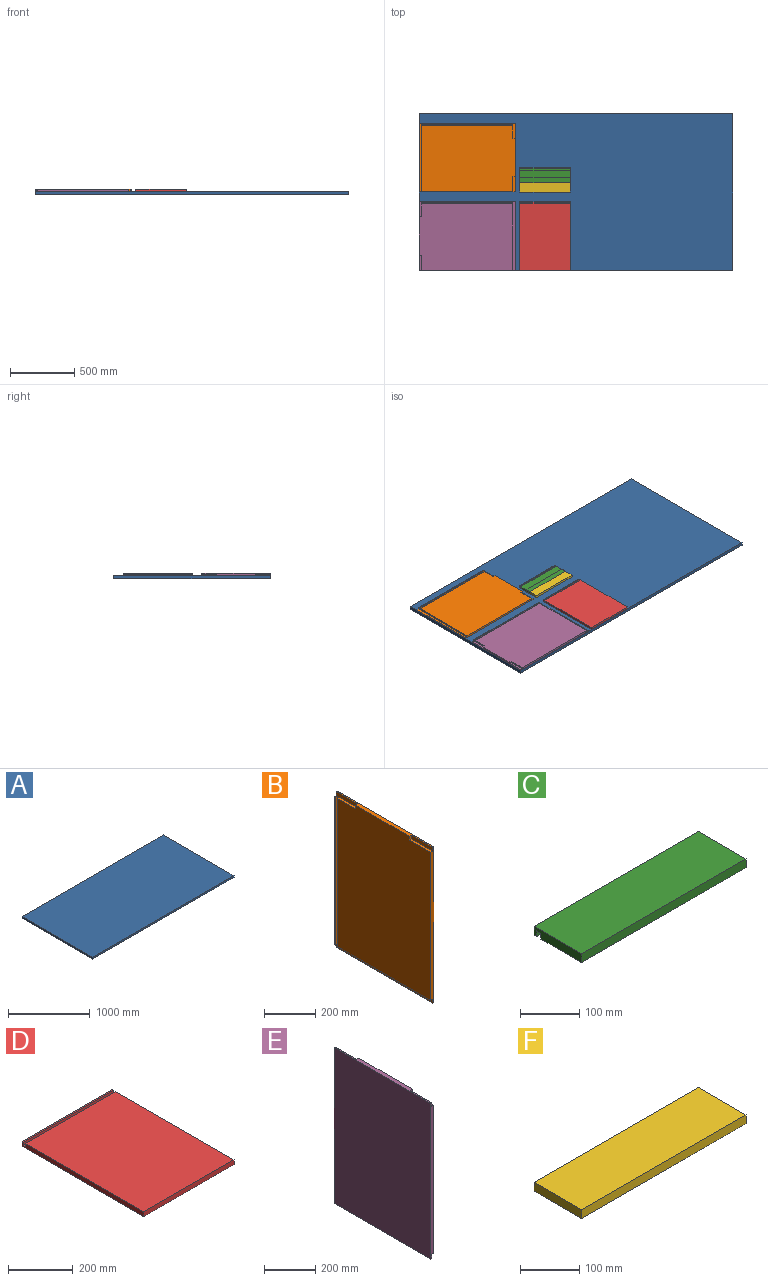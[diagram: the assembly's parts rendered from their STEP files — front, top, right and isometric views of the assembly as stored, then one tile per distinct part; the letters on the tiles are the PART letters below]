
ASSEMBLY  parts=6 mates=9
PART A: 6 faces, bbox 2438.4x1219.2x25.4 mm
  f0: plane 1219.2x25.4mm, normal (-1,0,0), area 30967.7mm2, adj f1,f3,f4,f5
  f1: plane 2438.4x25.4mm, normal (0,-1,0), area 61935.4mm2, adj f0,f2,f4,f5
  f2: plane 1219.2x25.4mm, normal (1,0,0), area 30967.7mm2, adj f1,f3,f4,f5
  f3: plane 2438.4x25.4mm, normal (0,1,0), area 61935.4mm2, adj f0,f2,f4,f5
  f4: plane 2438.4x1219.2mm, normal (0,0,-1), area 2972897.3mm2, adj f0,f1,f2,f3
  f5: plane 2438.4x1219.2mm, normal (0,0,1), area 2972897.3mm2, adj f0,f1,f2,f3
PART B: 18 faces, bbox 18.3x533.4x745.5 mm
  f0: plane 727.2x517.02mm, normal (-1,0,0), area 371978.6mm2, adj f1,f2,f4,f5,f11,f13,f14,f16
  f1: plane 517.02x11.94mm, normal (0,0,-1), area 6172.1mm2, adj f0,f4,f9,f16
  f2: plane 101.09x11.94mm, normal (0,0,1), area 1206.8mm2, adj f0,f9,f14,f16
  f3: plane 745.49x18.29mm, normal (0,1,0), area 13196.9mm2, adj f5,f6,f7,f8,f9,f10,f15
  f4: plane 745.49x18.29mm, normal (0,-1,0), area 13196.9mm2, adj f0,f1,f5,f7,f8,f9,f12,f13
  f5: plane 533.4x18.29mm, normal (0,0,1), area 6950mm2, adj f0,f3,f4,f7,f9,f11,f12,f14
  f6: plane 708.91x6.35mm, normal (-1,0,0), area 4501.6mm2, adj f3,f10,f15,f17
  f7: plane 745.49x533.4mm, normal (1,0,0), area 397644.4mm2, adj f3,f4,f5,f8
  f8: plane 533.4x6.35mm, normal (0,0,-1), area 3387.1mm2, adj f3,f4,f7,f9
  f9: plane 745.49x533.4mm, normal (-1,0,0), area 19015.7mm2, adj f1,f2,f3,f4,f5,f8,f10,f14
  f10: plane 11.94x6.35mm, normal (0,0,-1), area 75.8mm2, adj f3,f6,f9,f17
  f11: plane 18.29x11.94mm, normal (0,-1,0), area 218.3mm2, adj f0,f5,f12,f13
  f12: plane 117.48x18.29mm, normal (-1,0,0), area 2148.4mm2, adj f4,f5,f11,f13
  f13: plane 117.48x11.94mm, normal (0,0,1), area 1402.4mm2, adj f0,f4,f11,f12
  f14: plane 18.29x11.94mm, normal (0,1,0), area 218.3mm2, adj f0,f2,f5,f9
  f15: plane 11.94x6.35mm, normal (0,0,1), area 75.8mm2, adj f3,f6,f9,f17
  f16: plane 708.91x11.94mm, normal (0,1,0), area 8463mm2, adj f0,f1,f2,f9
  f17: plane 708.91x11.94mm, normal (0,-1,0), area 8463mm2, adj f6,f9,f10,f15
PART C: 10 faces, bbox 393.7x114.3x18.3 mm
  f0: plane 393.7x97.92mm, normal (0,0,-1), area 38549.9mm2, adj f2,f3,f4,f7
  f1: plane 393.7x18.29mm, normal (0,1,0), area 7200mm2, adj f2,f4,f5,f6
  f2: plane 114.3x18.29mm, normal (-1,0,0), area 1970.5mm2, adj f0,f1,f3,f5,f6,f7,f8,f9
  f3: plane 393.7x18.29mm, normal (0,-1,0), area 7200mm2, adj f0,f2,f4,f6
  f4: plane 114.3x18.29mm, normal (1,0,0), area 1970.5mm2, adj f0,f1,f3,f5,f6,f7,f8,f9
  f5: plane 393.7x6.35mm, normal (0,0,-1), area 2500mm2, adj f1,f2,f4,f8
  f6: plane 393.7x114.3mm, normal (0,0,1), area 44999.9mm2, adj f1,f2,f3,f4
  f7: plane 393.7x11.94mm, normal (0,1,0), area 4700mm2, adj f0,f2,f4,f9
  f8: plane 393.7x11.94mm, normal (0,-1,0), area 4700mm2, adj f2,f4,f5,f9
  f9: plane 393.7x10.03mm, normal (0,0,-1), area 3950mm2, adj f2,f4,f7,f8
PART D: 10 faces, bbox 393.7x533.4x18.3 mm
  f0: plane 517.02x393.7mm, normal (0,0,1), area 203549.6mm2, adj f1,f2,f3,f8
  f1: plane 533.4x18.29mm, normal (-1,0,0), area 9635mm2, adj f0,f2,f4,f5,f6,f7,f8,f9
  f2: plane 393.7x18.29mm, normal (0,-1,0), area 7200mm2, adj f0,f1,f3,f6
  f3: plane 533.4x18.29mm, normal (1,0,0), area 9635mm2, adj f0,f2,f4,f5,f6,f7,f8,f9
  f4: plane 393.7x18.29mm, normal (0,1,0), area 7200mm2, adj f1,f3,f5,f6
  f5: plane 393.7x6.35mm, normal (0,0,1), area 2500mm2, adj f1,f3,f4,f9
  f6: plane 533.4x393.7mm, normal (0,0,-1), area 209999.6mm2, adj f1,f2,f3,f4
  f7: plane 393.7x10.03mm, normal (0,0,1), area 3950mm2, adj f1,f3,f8,f9
  f8: plane 393.7x11.94mm, normal (0,1,0), area 4700mm2, adj f0,f1,f3,f7
  f9: plane 393.7x11.94mm, normal (0,-1,0), area 4700mm2, adj f1,f3,f5,f7
PART E: 18 faces, bbox 18.3x533.4x745.5 mm
  f0: plane 727.2x517.02mm, normal (1,0,0), area 371978.6mm2, adj f1,f2,f4,f7,f11,f12,f14,f16
  f1: plane 517.02x11.94mm, normal (0,0,-1), area 6172.1mm2, adj f0,f7,f10,f16
  f2: plane 101.09x11.94mm, normal (0,0,1), area 1206.8mm2, adj f0,f10,f14,f16
  f3: plane 745.49x18.29mm, normal (0,1,0), area 13196.9mm2, adj f4,f5,f6,f8,f9,f10,f15
  f4: plane 533.4x18.29mm, normal (0,0,1), area 6950mm2, adj f0,f3,f7,f8,f10,f11,f13,f14
  f5: plane 708.91x6.35mm, normal (1,0,0), area 4501.6mm2, adj f3,f9,f15,f17
  f6: plane 533.4x6.35mm, normal (0,0,-1), area 3387.1mm2, adj f3,f7,f8,f10
  f7: plane 745.49x18.29mm, normal (0,-1,0), area 13196.9mm2, adj f0,f1,f4,f6,f8,f10,f12,f13
  f8: plane 745.49x533.4mm, normal (-1,0,0), area 397644.4mm2, adj f3,f4,f6,f7
  f9: plane 11.94x6.35mm, normal (0,0,-1), area 75.8mm2, adj f3,f5,f10,f17
  f10: plane 745.49x533.4mm, normal (1,0,0), area 19015.7mm2, adj f1,f2,f3,f4,f6,f7,f9,f14
  f11: plane 18.29x11.94mm, normal (0,-1,0), area 218.3mm2, adj f0,f4,f12,f13
  f12: plane 117.48x11.94mm, normal (0,0,1), area 1402.4mm2, adj f0,f7,f11,f13
  f13: plane 117.48x18.29mm, normal (1,0,0), area 2148.4mm2, adj f4,f7,f11,f12
  f14: plane 18.29x11.94mm, normal (0,1,0), area 218.3mm2, adj f0,f2,f4,f10
  f15: plane 11.94x6.35mm, normal (0,0,1), area 75.8mm2, adj f3,f5,f10,f17
  f16: plane 708.91x11.94mm, normal (0,1,0), area 8463mm2, adj f0,f1,f2,f10
  f17: plane 708.91x11.94mm, normal (0,-1,0), area 8463mm2, adj f5,f9,f10,f15
PART F: 6 faces, bbox 393.7x114.3x18.3 mm
  f0: plane 393.7x18.29mm, normal (0,1,0), area 7200mm2, adj f1,f3,f4,f5
  f1: plane 114.3x18.29mm, normal (-1,0,0), area 2090.3mm2, adj f0,f2,f4,f5
  f2: plane 393.7x18.29mm, normal (0,-1,0), area 7200mm2, adj f1,f3,f4,f5
  f3: plane 114.3x18.29mm, normal (1,0,0), area 2090.3mm2, adj f0,f2,f4,f5
  f4: plane 393.7x114.3mm, normal (0,0,-1), area 44999.9mm2, adj f0,f1,f2,f3
  f5: plane 393.7x114.3mm, normal (0,0,1), area 44999.9mm2, adj f0,f1,f2,f3
PLACE A at identity fixed
PLACE B rot(axis=(0,1,0),90deg) t=(0,609.6,406.4)mm
PLACE C rot(axis=(0,1,0),180deg) t=(1181.88,263.46,745.49)mm
PLACE D t=(775.48,0,0)mm
PLACE E rot(axis=(0,-1,0),90deg) t=(745.49,0,0)mm
PLACE F t=(775.48,609.22,-727.2)mm
MATE planar F.f4 <-> A.f5  axis (0,0,-1) through (978.68,723.52,0)mm
MATE planar A.f1 <-> D.f2  axis (0,-1,0) through (1219.2,0,-12.7)mm
MATE slider E.f6 <-> D.f1  axis (1,0,0) through (745.49,0,0)mm
MATE fastened B.f7 <-> A.f5  axis (0,0,-1) through (0,609.6,0)mm
MATE planar C.f4 <-> F.f1  axis (-1,0,0) through (781.83,736.93,8.95)mm
MATE planar F.f1 <-> D.f1  axis (-1,0,0) through (781.83,666.37,9.14)mm
MATE fastened E.f8 <-> A.f5  axis (0,0,-1) through (0,0,0)mm
MATE planar A.f5 <-> D.f6  axis (0,0,1) through (1219.2,609.6,0)mm
MATE planar A.f5 <-> C.f6  axis (0,0,1) through (1219.2,1219.2,0)mm
